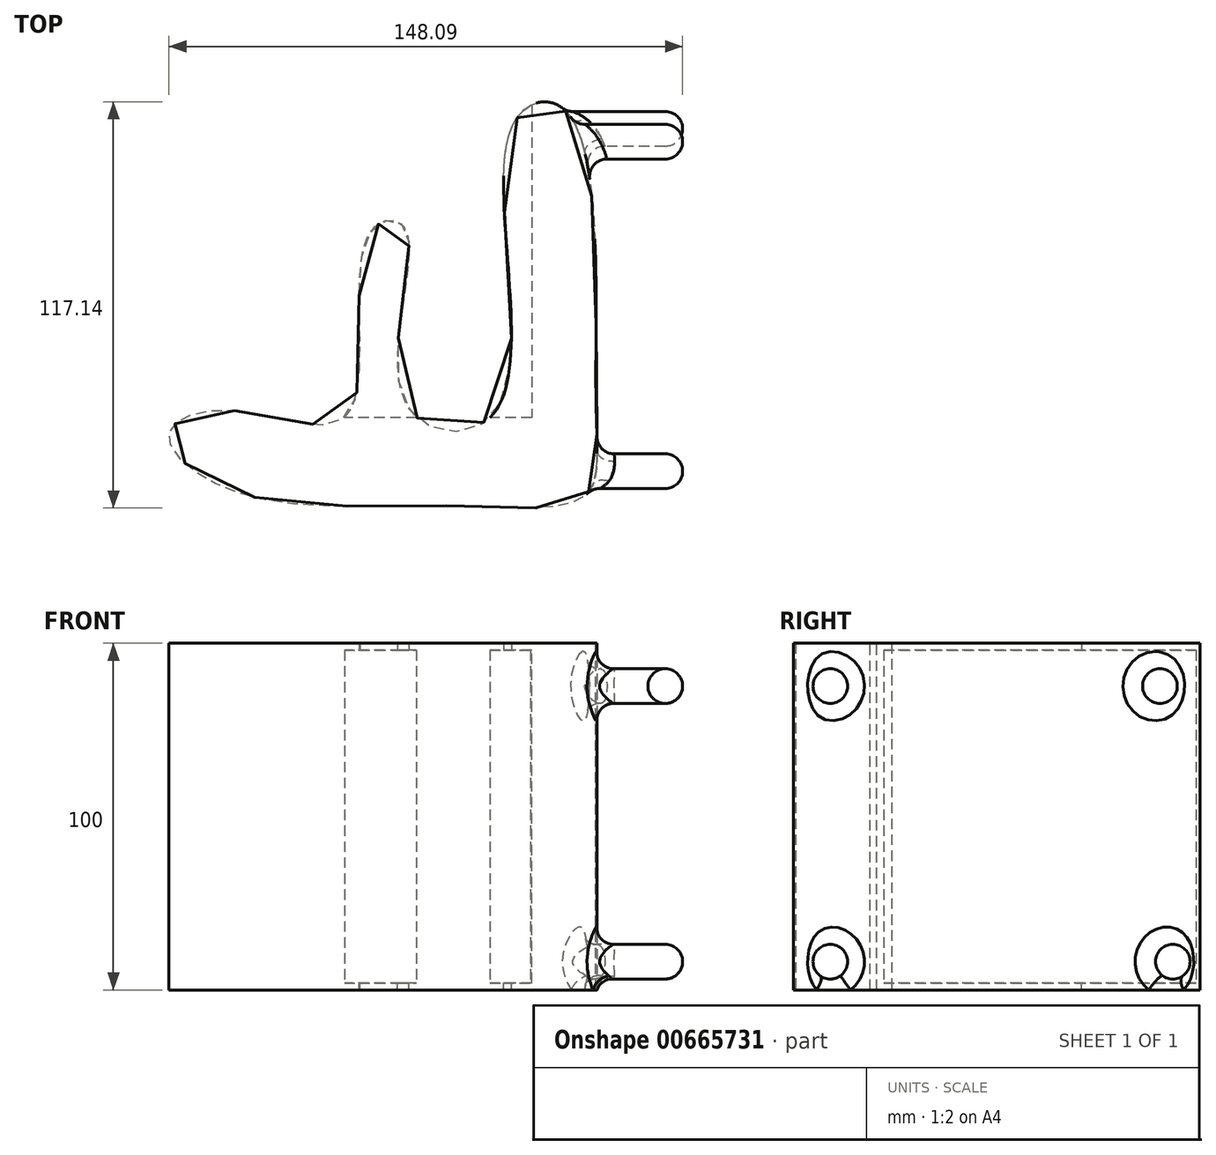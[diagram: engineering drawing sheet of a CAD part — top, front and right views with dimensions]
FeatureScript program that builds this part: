
annotation { "Feature Type Name" : "Feature", "Feature Type Description" : "" }
export const myFeature = defineFeature(function(context is Context, id is Id, definition is map)
    precondition{}
    {
        {
            var Q0;
            Q0=qCreatedBy(makeId("Top.planeOp"),FACE);
            var sketch = newSketch(context, id + "F0", { "sketchPlane" : qUnion([Q0])});
            skFitSpline(sketch, "E0", {"points": [v(-49.17, -32.93) * mm, v(-16.39, -33.86) * mm, v(-10.51, 17.78) * mm, v(0, 19.64) * mm, v(0, -30.77) * mm, v(25.97, -33.24) * mm, v(30.61, 48.4) * mm, v(46.38, 53.34) * mm, v(55.04, -30.77) * mm, v(51.33, -57.98) * mm, v(12.06, -60.45) * mm, v(-49.78, -56.12) * mm, v(-68.03, -39.73) * mm, v(-49.17, -32.93) * mm]});
            skSolve(sketch);
        }
        {
            var Q0;
            Q0 = qSketchRegion(id + "F0", true);
            extrude(context, id + "F1", {"entities" : qUnion([Q0]), "depth" : 50 * mm, "offsetDistance" : 25 * mm});
        }
        {
            var Q0;
            Q0=makeQuery(id+"F1.opExtrude","SWEPT_BODY",BODY,{"disambiguationData":[OSD([sQuery(id+"F0.wireOp",EDGE,"E0")])]});
            var Q1;
            Q1=qCreatedBy(makeId("Top.planeOp"),FACE);
            mirror(context, id + "F2", {"operationType" : NewBodyOperationType.ADD, "entities" : qUnion([Q0]), "mirrorPlane" : qUnion([Q1])});
        }
        {
            var Q0;
            Q0=qCreatedBy(makeId("Right.planeOp"),FACE);
            var sketch = newSketch(context, id + "F3", { "sketchPlane" : qUnion([Q0])});
            skCircle(sketch, "E1", {"center": v(-50.46, -41.85) * mm, "radius": 5 * mm});
            skPoint(sketch, "E1.centerSnap0", {"position": v(-50.46, -46.85) * mm});
            skPoint(sketch, "E1.centerSnap1", {"position": v(-55.46, -41.85) * mm});
            skCircle(sketch, "E2", {"center": v(-50.46, 37.62) * mm, "radius": 5 * mm});
            skPoint(sketch, "E2.centerSnap0", {"position": v(-50.46, 42.62) * mm});
            skPoint(sketch, "E2.centerSnap1", {"position": v(-45.46, 37.62) * mm});
            skCircle(sketch, "E3", {"center": v(44.58, 37.62) * mm, "radius": 5 * mm});
            skPoint(sketch, "E3.centerSnap0", {"position": v(49.58, 37.62) * mm});
            skPoint(sketch, "E3.centerSnap1", {"position": v(44.58, 42.62) * mm});
            skCircle(sketch, "E4", {"center": v(48.3, -41.85) * mm, "radius": 5 * mm});
            skPoint(sketch, "E4.centerSnap0", {"position": v(48.3, -47.16) * mm});
            skPoint(sketch, "E5.orphan", {"position": v(-55.46, -36.85) * mm});
            skPoint(sketch, "E6.orphan", {"position": v(-45.46, -36.85) * mm});
            skPoint(sketch, "E7.orphan", {"position": v(-45.46, -46.85) * mm});
            skPoint(sketch, "E8.left.start.orphan", {"position": v(-55.46, -46.85) * mm});
            skPoint(sketch, "E9.orphan", {"position": v(-45.46, 32.62) * mm});
            skPoint(sketch, "E10.orphan", {"position": v(-45.46, 42.62) * mm});
            skPoint(sketch, "E11.left.start.orphan", {"position": v(-55.46, 42.62) * mm});
            skPoint(sketch, "E12.orphan", {"position": v(39.58, 42.62) * mm});
            skPoint(sketch, "E13.orphan", {"position": v(49.58, 42.62) * mm});
            skPoint(sketch, "E14.orphan", {"position": v(49.58, 32.62) * mm});
            skPoint(sketch, "E15.top.end.orphan", {"position": v(39.58, 32.62) * mm});
            skPoint(sketch, "E16.orphan", {"position": v(43.3, -47.16) * mm});
            skPoint(sketch, "E17.orphan", {"position": v(53.3, -47.16) * mm});
            skSolve(sketch);
        }
        {
            var Q0;
            Q0 = qSketchRegion(id + "F3", true);
            extrude(context, id + "F4", {"entities" : qUnion([Q0]), "operationType" : NewBodyOperationType.ADD, "depth" : 80 * mm, "offsetDistance" : 25 * mm});
        }
        {
            var Q0;
            Q0=qCreatedBy(makeId("Front.planeOp"),FACE);
            var sketch = newSketch(context, id + "F5", { "sketchPlane" : qUnion([Q0])});
            skLineSegment(sketch, "E18.bottom", {"start": v(36.5, 48) * mm, "end": v(-36.5, 48) * mm});
            skLineSegment(sketch, "E18.top", {"start": v(36.5, -48) * mm, "end": v(-36.5, -48) * mm});
            skLineSegment(sketch, "E18.left", {"start": v(36.5, 48) * mm, "end": v(36.5, -48) * mm});
            skLineSegment(sketch, "E18.right", {"start": v(-36.5, 48) * mm, "end": v(-36.5, -48) * mm});
            skPoint(sketch, "E18.middle", {"position": v(0, 0) * mm});
            skSolve(sketch);
        }
        {
            var Q0;
            Q0 = qSketchRegion(id + "F5", true);
            extrude(context, id + "F6", {"entities" : qUnion([Q0]), "operationType" : NewBodyOperationType.REMOVE, "oppositeDirection" : true, "depth" : 55 * mm, "offsetDistance" : 25 * mm});
        }
        {
            var Q0;
            Q0=qCreatedBy(makeId("Front.planeOp"),FACE);
            var sketch = newSketch(context, id + "F7", { "sketchPlane" : qUnion([Q0])});
            skLineSegment(sketch, "E19.bottom", {"start": v(36.5, -48) * mm, "end": v(-36.5, -48) * mm});
            skLineSegment(sketch, "E19.top", {"start": v(36.5, 48) * mm, "end": v(-36.5, 48) * mm});
            skLineSegment(sketch, "E19.left", {"start": v(36.5, -48) * mm, "end": v(36.5, 48) * mm});
            skLineSegment(sketch, "E19.right", {"start": v(-36.5, -48) * mm, "end": v(-36.5, 48) * mm});
            skPoint(sketch, "E19.middle", {"position": v(0, 0) * mm});
            skSolve(sketch);
        }
        {
            var Q0;
            Q0 = qSketchRegion(id + "F7", true);
            extrude(context, id + "F8", {"entities" : qUnion([Q0]), "operationType" : NewBodyOperationType.REMOVE, "depth" : 35 * mm, "offsetDistance" : 25 * mm});
        }
        {
            var Q0;
            Q0=makeQuery(id+"F4.opExtrude","SWEPT_FACE",FACE,{"disambiguationData":[OSD([sQuery(id+"F3.wireOp",EDGE,"E2")])]});
            var Q1;
            {var subQ1=sQuery(id+"F3.wireOp",EDGE,"E3");Q1=makeQuery(id+"F4.boolean.opBoolean","SPLIT",FACE,{"disambiguationData":[TD([makeQuery(id+"F4.opExtrude","CAP_FACE",FACE,{"disambiguationData":[OSD([subQ1])],"isStart":false})])],"derivedFrom":makeQuery(id+"F4.opExtrude","SWEPT_FACE",FACE,{"disambiguationData":[OSD([subQ1])]})});}
            var Q2;
            Q2=makeQuery(id+"F4.opExtrude","CAP_EDGE",EDGE,{"disambiguationData":[OSD([sQuery(id+"F3.wireOp",EDGE,"E2")])],"isStart":false});
            var Q3;
            {var subQ0=makeQuery(id+"F1.opExtrude","SWEPT_FACE",FACE,{"disambiguationData":[OSD([sQuery(id+"F0.wireOp",EDGE,"E0")])]});Q3=makeQuery(id+"F4.boolean.opBoolean","INTERSECT",EDGE,{"derivedFrom":[makeQuery(id+"F2.boolean.opBoolean","MERGE",FACE,{"derivedFrom":[subQ0,makeQuery(id+"F2.opPattern","COPY",FACE,{"derivedFrom":subQ0,"instanceName":"1"})]}),makeQuery(id+"F4.opExtrude","SWEPT_FACE",FACE,{"disambiguationData":[OSD([sQuery(id+"F3.wireOp",EDGE,"E2")])]})]});}
            var Q4;
            Q4=makeQuery(id+"F4.opExtrude","CAP_FACE",FACE,{"disambiguationData":[OSD([sQuery(id+"F3.wireOp",EDGE,"E3")])],"isStart":false});
            var Q5;
            {var subQ0=makeQuery(id+"F1.opExtrude","SWEPT_FACE",FACE,{"disambiguationData":[OSD([sQuery(id+"F0.wireOp",EDGE,"E0")])]});Q5=makeQuery(id+"F4.boolean.opBoolean","INTERSECT",EDGE,{"disambiguationData":[OD(1.0)],"derivedFrom":[makeQuery(id+"F2.boolean.opBoolean","MERGE",FACE,{"derivedFrom":[subQ0,makeQuery(id+"F2.opPattern","COPY",FACE,{"derivedFrom":subQ0,"instanceName":"1"})]}),makeQuery(id+"F4.opExtrude","SWEPT_FACE",FACE,{"disambiguationData":[OSD([sQuery(id+"F3.wireOp",EDGE,"E3")])]})]});}
            var Q6;
            Q6=makeQuery(id+"F4.opExtrude","CAP_EDGE",EDGE,{"disambiguationData":[OSD([sQuery(id+"F3.wireOp",EDGE,"E1")])],"isStart":false});
            var Q7;
            {var subQ0=makeQuery(id+"F1.opExtrude","SWEPT_FACE",FACE,{"disambiguationData":[OSD([sQuery(id+"F0.wireOp",EDGE,"E0")])]});Q7=makeQuery(id+"F4.boolean.opBoolean","INTERSECT",EDGE,{"derivedFrom":[makeQuery(id+"F2.boolean.opBoolean","MERGE",FACE,{"derivedFrom":[subQ0,makeQuery(id+"F2.opPattern","COPY",FACE,{"derivedFrom":subQ0,"instanceName":"1"})]}),makeQuery(id+"F4.opExtrude","SWEPT_FACE",FACE,{"disambiguationData":[OSD([sQuery(id+"F3.wireOp",EDGE,"E1")])]})]});}
            var Q8;
            Q8=makeQuery(id+"F4.opExtrude","CAP_EDGE",EDGE,{"disambiguationData":[OSD([sQuery(id+"F3.wireOp",EDGE,"E4")])],"isStart":false});
            var Q9;
            {var subQ0=makeQuery(id+"F1.opExtrude","SWEPT_FACE",FACE,{"disambiguationData":[OSD([sQuery(id+"F0.wireOp",EDGE,"E0")])]});Q9=makeQuery(id+"F4.boolean.opBoolean","INTERSECT",EDGE,{"disambiguationData":[OD(1.0)],"derivedFrom":[makeQuery(id+"F2.boolean.opBoolean","MERGE",FACE,{"derivedFrom":[subQ0,makeQuery(id+"F2.opPattern","COPY",FACE,{"derivedFrom":subQ0,"instanceName":"1"})]}),makeQuery(id+"F4.opExtrude","SWEPT_FACE",FACE,{"disambiguationData":[OSD([sQuery(id+"F3.wireOp",EDGE,"E4")])]})]});}
            fillet(context, id + "F9", {"entities" : qUnion([Q0, Q1, Q2, Q3, Q4, Q5, Q6, Q7, Q8, Q9]), "radius" : 5 * mm, "tangentPropagation" : true, "allowEdgeOverflow" : false});
        }
    });
